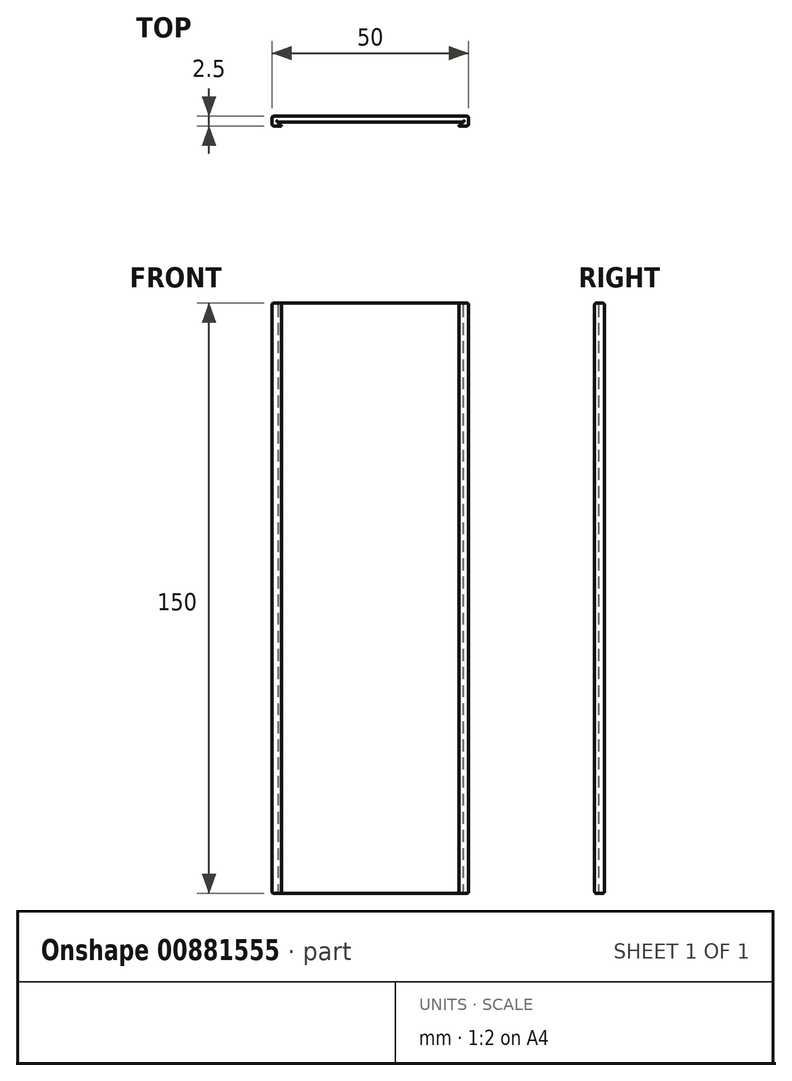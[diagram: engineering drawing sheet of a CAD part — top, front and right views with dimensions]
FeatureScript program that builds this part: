
annotation { "Feature Type Name" : "Feature", "Feature Type Description" : "" }
export const myFeature = defineFeature(function(context is Context, id is Id, definition is map)
    precondition{}
    {
        {
            var Q0;
            Q0=qCreatedBy(makeId("Top.planeOp"),FACE);
            var sketch = newSketch(context, id + "F0", { "sketchPlane" : qUnion([Q0])});
            skLineSegment(sketch, "E0", {"start": v(0, 0) * mm, "end": v(47, 0) * mm});
            skLineSegment(sketch, "E1", {"start": v(47, 0) * mm, "end": v(46, -1) * mm});
            skLineSegment(sketch, "E2", {"start": v(46, -1) * mm, "end": v(48.5, -1) * mm});
            skLineSegment(sketch, "E3", {"start": v(48.5, -1) * mm, "end": v(48.5, 1.5) * mm});
            skLineSegment(sketch, "E4", {"start": v(48.5, 1.5) * mm, "end": v(-1.5, 1.5) * mm});
            skLineSegment(sketch, "E5", {"start": v(-1.5, 1.5) * mm, "end": v(-1.5, -1) * mm});
            skLineSegment(sketch, "E6", {"start": v(-1.5, -1) * mm, "end": v(1, -1) * mm});
            skLineSegment(sketch, "E7", {"start": v(1, -1) * mm, "end": v(0, 0) * mm});
            skSolve(sketch);
        }
        {
            var Q0;
            Q0=makeQuery(id+"F0.imprint","IMPRINT",FACE,{"disambiguationData":[TD([[makeQuery(id+"F0.imprint","IMPRINT",EDGE,{"derivedFrom":sQuery(id+"F0.wireOp",EDGE,"E0")}),1.0]])]});
            extrude(context, id + "F1", {"entities" : qUnion([Q0]), "depth" : 150 * mm, "offsetDistance" : 25 * mm});
        }
        {
            var Q0;
            Q0=makeQuery(id+"F1.opExtrude","CAP_EDGE",EDGE,{"disambiguationData":[OSD([sQuery(id+"F0.wireOp",EDGE,"E0")])],"isStart":false});
            var Q1;
            Q1=makeQuery(id+"F1.opExtrude","CAP_EDGE",EDGE,{"disambiguationData":[OSD([sQuery(id+"F0.wireOp",EDGE,"E4")])],"isStart":false});
            var Q2;
            Q2=makeQuery(id+"F1.opExtrude","CAP_EDGE",EDGE,{"disambiguationData":[OSD([sQuery(id+"F0.wireOp",EDGE,"E5")])],"isStart":false});
            var Q3;
            Q3=makeQuery(id+"F1.opExtrude","CAP_EDGE",EDGE,{"disambiguationData":[OSD([sQuery(id+"F0.wireOp",EDGE,"E3")])],"isStart":false});
            var Q4;
            Q4=makeQuery(id+"F1.opExtrude","SWEPT_EDGE",EDGE,{"disambiguationData":[OSD([sQuery(id+"F0.wireOp",EDGE,"E2"),sQuery(id+"F0.wireOp",EDGE,"E3")])]});
            var Q5;
            Q5=makeQuery(id+"F1.opExtrude","SWEPT_EDGE",EDGE,{"disambiguationData":[OSD([sQuery(id+"F0.wireOp",EDGE,"E3"),sQuery(id+"F0.wireOp",EDGE,"E4")])]});
            var Q6;
            Q6=makeQuery(id+"F1.opExtrude","CAP_EDGE",EDGE,{"disambiguationData":[OSD([sQuery(id+"F0.wireOp",EDGE,"E3")])],"isStart":true});
            var Q7;
            Q7=makeQuery(id+"F1.opExtrude","SWEPT_EDGE",EDGE,{"disambiguationData":[OSD([sQuery(id+"F0.wireOp",EDGE,"E5"),sQuery(id+"F0.wireOp",EDGE,"E6")])]});
            var Q8;
            Q8=makeQuery(id+"F1.opExtrude","SWEPT_EDGE",EDGE,{"disambiguationData":[OSD([sQuery(id+"F0.wireOp",EDGE,"E4"),sQuery(id+"F0.wireOp",EDGE,"E5")])]});
            var Q9;
            Q9=makeQuery(id+"F1.opExtrude","CAP_EDGE",EDGE,{"disambiguationData":[OSD([sQuery(id+"F0.wireOp",EDGE,"E4")])],"isStart":true});
            var Q10;
            Q10=makeQuery(id+"F1.opExtrude","CAP_EDGE",EDGE,{"disambiguationData":[OSD([sQuery(id+"F0.wireOp",EDGE,"E5")])],"isStart":true});
            var Q11;
            Q11=makeQuery(id+"F1.opExtrude","CAP_EDGE",EDGE,{"disambiguationData":[OSD([sQuery(id+"F0.wireOp",EDGE,"E2")])],"isStart":true});
            var Q12;
            Q12=makeQuery(id+"F1.opExtrude","CAP_EDGE",EDGE,{"disambiguationData":[OSD([sQuery(id+"F0.wireOp",EDGE,"E6")])],"isStart":true});
            var Q13;
            Q13=makeQuery(id+"F1.opExtrude","CAP_EDGE",EDGE,{"disambiguationData":[OSD([sQuery(id+"F0.wireOp",EDGE,"E0")])],"isStart":true});
            var Q14;
            Q14=makeQuery(id+"F1.opExtrude","CAP_EDGE",EDGE,{"disambiguationData":[OSD([sQuery(id+"F0.wireOp",EDGE,"E6")])],"isStart":false});
            var Q15;
            Q15=makeQuery(id+"F1.opExtrude","CAP_EDGE",EDGE,{"disambiguationData":[OSD([sQuery(id+"F0.wireOp",EDGE,"E2")])],"isStart":false});
            fillet(context, id + "F2", {"entities" : qUnion([Q0, Q1, Q2, Q3, Q4, Q5, Q6, Q7, Q8, Q9, Q10, Q11, Q12, Q13, Q14, Q15]), "radius" : 0.5 * mm, "tangentPropagation" : true, "allowEdgeOverflow" : false});
        }
    });
